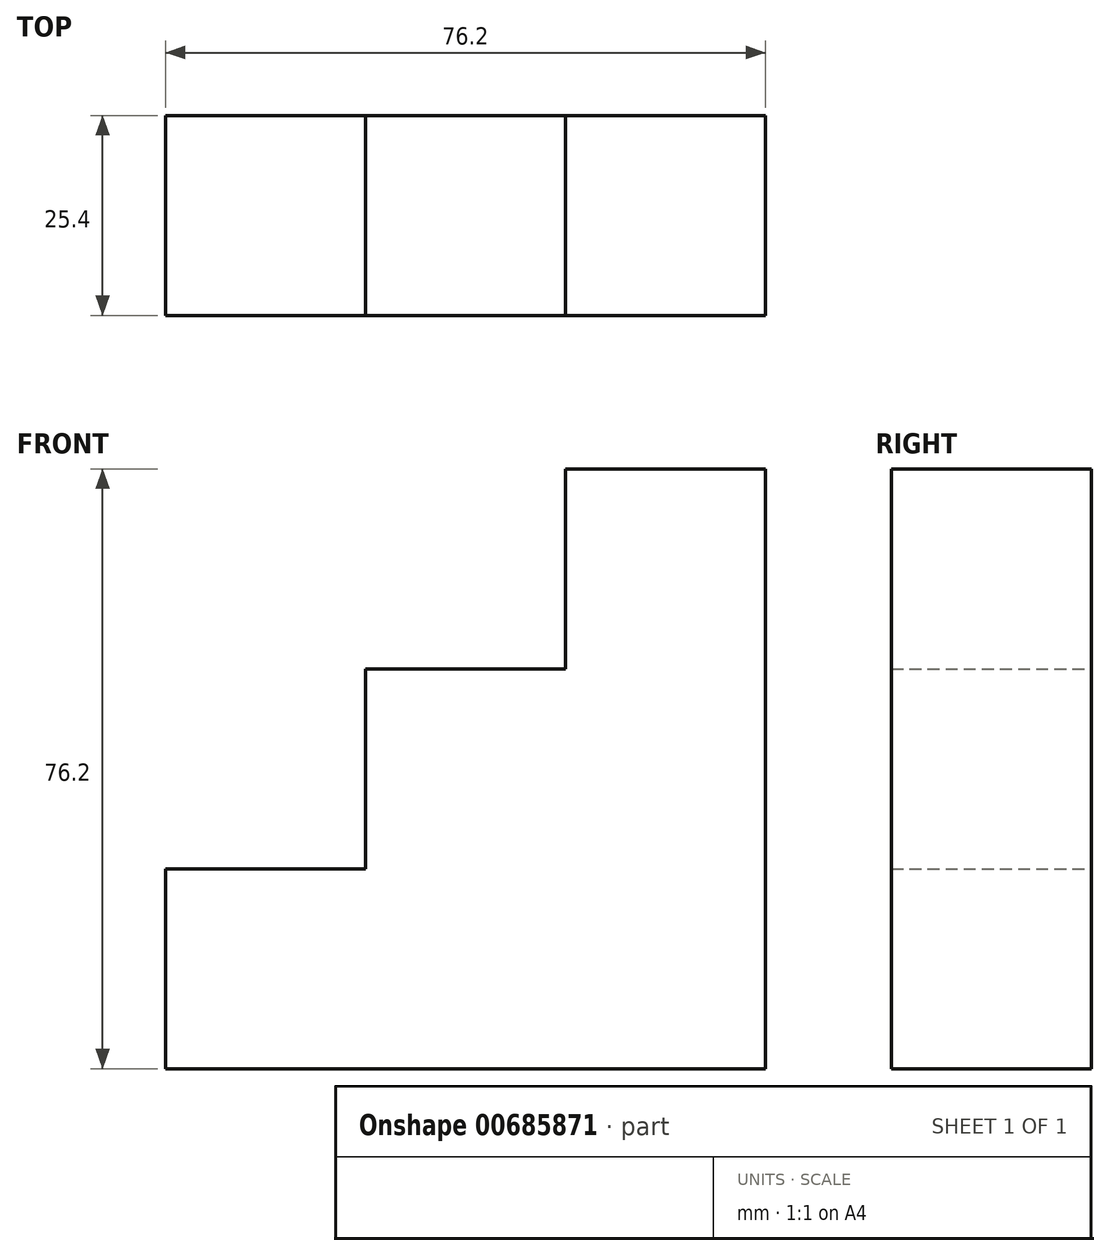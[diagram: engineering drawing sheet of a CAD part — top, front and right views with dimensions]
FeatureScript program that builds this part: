
annotation { "Feature Type Name" : "Feature", "Feature Type Description" : "" }
export const myFeature = defineFeature(function(context is Context, id is Id, definition is map)
    precondition{}
    {
        {
            var Q0;
            Q0=qCreatedBy(makeId("Front.planeOp"),FACE);
            var sketch = newSketch(context, id + "F0", { "sketchPlane" : qUnion([Q0])});
            skLineSegment(sketch, "E0", {"start": v(0, 0) * mm, "end": v(76.2, 0) * mm});
            skLineSegment(sketch, "E1", {"start": v(76.2, 0) * mm, "end": v(76.2, 76.2) * mm});
            skLineSegment(sketch, "E2", {"start": v(76.2, 76.2) * mm, "end": v(50.81, 76.2) * mm});
            skLineSegment(sketch, "E3", {"start": v(50.81, 76.2) * mm, "end": v(50.81, 50.8) * mm});
            skLineSegment(sketch, "E4", {"start": v(50.81, 50.8) * mm, "end": v(25.41, 50.8) * mm});
            skLineSegment(sketch, "E5", {"start": v(25.41, 50.8) * mm, "end": v(25.41, 25.4) * mm});
            skLineSegment(sketch, "E6", {"start": v(25.41, 25.4) * mm, "end": v(0.01, 25.4) * mm});
            skLineSegment(sketch, "E7", {"start": v(0.01, 25.4) * mm, "end": v(0, 25.4) * mm});
            skLineSegment(sketch, "E8", {"start": v(0, 25.4) * mm, "end": v(0, 0) * mm});
            skSolve(sketch);
        }
        {
            var Q0;
            Q0=makeQuery(id+"F0.imprint","IMPRINT",FACE,{"disambiguationData":[TD([[makeQuery(id+"F0.imprint","IMPRINT",EDGE,{"derivedFrom":sQuery(id+"F0.wireOp",EDGE,"E0")}),1.0]])]});
            extrude(context, id + "F1", {"entities" : qUnion([Q0]), "depth" : 25.4 * mm, "offsetDistance" : 25.4 * mm});
        }
    });
